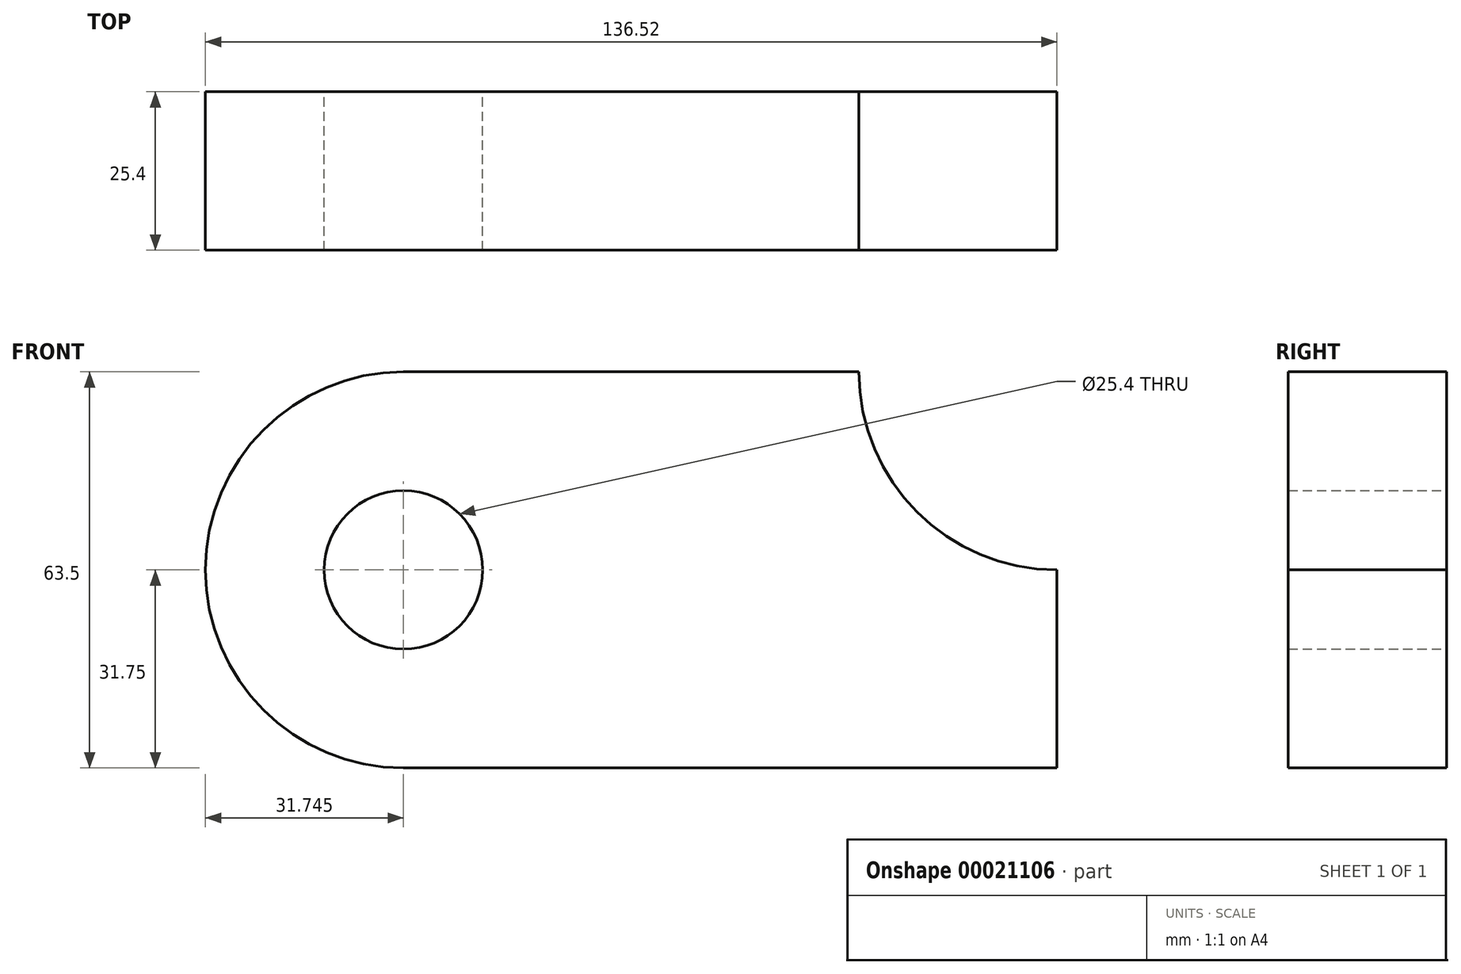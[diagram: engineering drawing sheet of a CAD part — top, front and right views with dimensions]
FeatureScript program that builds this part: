
annotation { "Feature Type Name" : "Feature", "Feature Type Description" : "" }
export const myFeature = defineFeature(function(context is Context, id is Id, definition is map)
    precondition{}
    {
        {
            var Q0;
            Q0=qCreatedBy(makeId("Front.planeOp"),FACE);
            var sketch = newSketch(context, id + "F0", { "sketchPlane" : qUnion([Q0])});
            skLineSegment(sketch, "E0.bottom", {"start": v(0, 0) * mm, "end": v(-104.77, 0) * mm});
            skLineSegment(sketch, "E0.top", {"start": v(0, 63.5) * mm, "end": v(-104.77, 63.5) * mm});
            skLineSegment(sketch, "E0.left", {"start": v(0, 0) * mm, "end": v(0, 63.5) * mm});
            skLineSegment(sketch, "E0.right", {"start": v(-104.77, 0) * mm, "end": v(-104.77, 63.5) * mm});
            skCircle(sketch, "E1", {"center": v(-104.77, 31.75) * mm, "radius": 31.75 * mm});
            skCircle(sketch, "E2", {"center": v(-104.77, 31.75) * mm, "radius": 12.7 * mm});
            skCircle(sketch, "E3", {"center": v(0, 63.5) * mm, "radius": 31.75 * mm});
            skSolve(sketch);
        }
        {
            var Q0;
            {var subQ4=sQuery(id+"F0.wireOp",EDGE,"E0.bottom");Q0=makeQuery(id+"F0.imprint","IMPRINT",FACE,{"disambiguationData":[TD([[makeQuery(id+"F0.imprint","IMPRINT",EDGE,{"derivedFrom":subQ4}),-1.0]])]});}
            var Q1;
            {var subQ0=sQuery(id+"F0.wireOp",EDGE,"E2");var subQ1=sQuery(id+"F0.wireOp",EDGE,"E0.right");var subQ3=makeQuery(id+"F0.imprint","INTERSECT",VERTEX,{"disambiguationData":[OD(0.0)],"derivedFrom":[subQ1,subQ0]});Q1=makeQuery(id+"F0.imprint","IMPRINT",FACE,{"disambiguationData":[TD([[makeQuery(id+"F0.imprint","IMPRINT",EDGE,{"disambiguationData":[TD([[subQ3,1.0]])],"derivedFrom":subQ0}),-1.0]])]});}
            var Q2;
            {var subQ0=sQuery(id+"F0.wireOp",EDGE,"E2");var subQ1=sQuery(id+"F0.wireOp",EDGE,"E0.right");var subQ3=makeQuery(id+"F0.imprint","INTERSECT",VERTEX,{"disambiguationData":[OD(0.0)],"derivedFrom":[subQ1,subQ0]});Q2=makeQuery(id+"F0.imprint","IMPRINT",FACE,{"disambiguationData":[TD([[makeQuery(id+"F0.imprint","IMPRINT",EDGE,{"disambiguationData":[TD([[subQ3,-1.0]])],"derivedFrom":subQ0}),-1.0]])]});}
            extrude(context, id + "F1", {"entities" : qUnion([Q0, Q1, Q2]), "depth" : 25.4 * mm});
        }
    });
